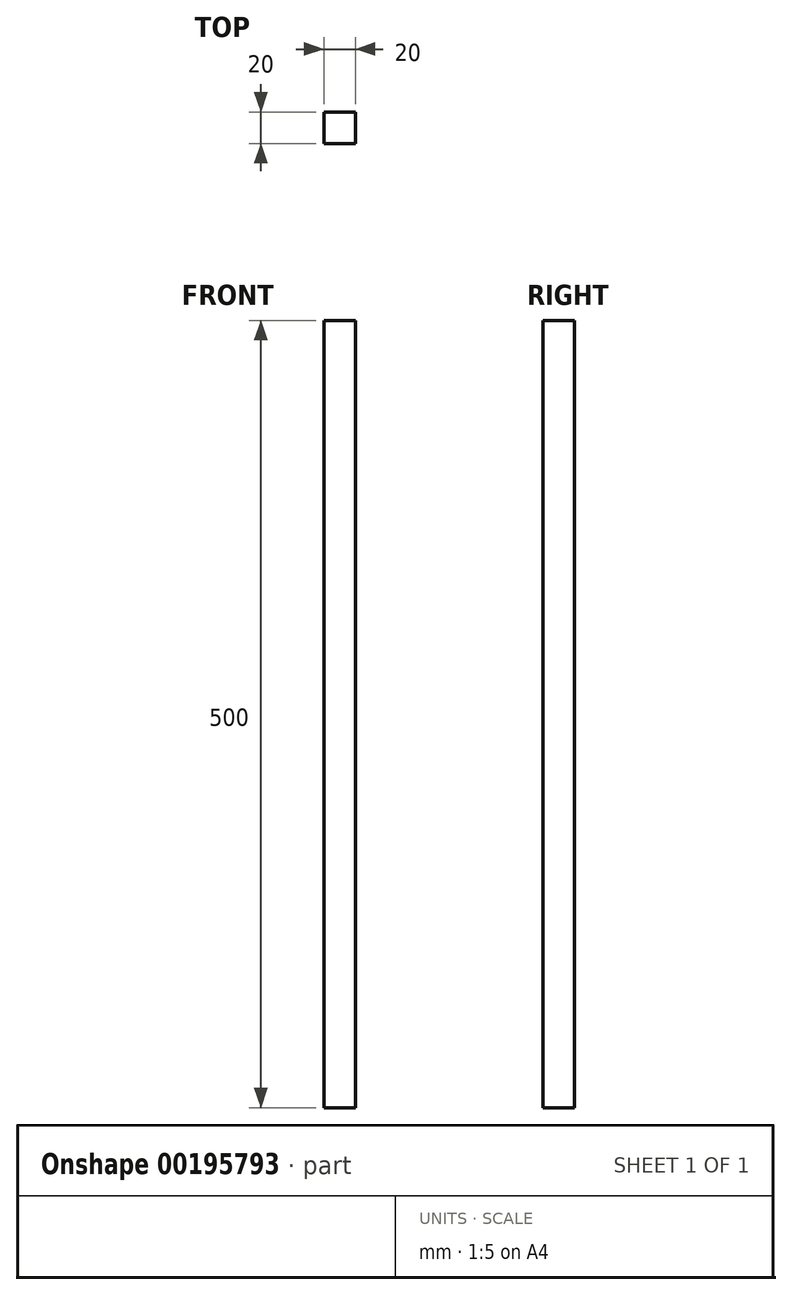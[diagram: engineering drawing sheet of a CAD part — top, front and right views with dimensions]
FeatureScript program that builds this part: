
annotation { "Feature Type Name" : "Feature", "Feature Type Description" : "" }
export const myFeature = defineFeature(function(context is Context, id is Id, definition is map)
    precondition{}
    {
        {
            var Q0;
            Q0=qCreatedBy(makeId("Top.planeOp"),FACE);
            var sketch = newSketch(context, id + "F0", { "sketchPlane" : qUnion([Q0])});
            skLineSegment(sketch, "E0.bottom", {"start": v(-80.54, -42.95) * mm, "end": v(-60.54, -42.95) * mm});
            skLineSegment(sketch, "E0.top", {"start": v(-80.54, -22.95) * mm, "end": v(-60.54, -22.95) * mm});
            skLineSegment(sketch, "E0.left", {"start": v(-80.54, -42.95) * mm, "end": v(-80.54, -22.95) * mm});
            skLineSegment(sketch, "E0.right", {"start": v(-60.54, -42.95) * mm, "end": v(-60.54, -22.95) * mm});
            skSolve(sketch);
        }
        {
            var Q0;
            Q0=makeQuery(id+"F0.imprint","IMPRINT",FACE,{"disambiguationData":[TD([[makeQuery(id+"F0.imprint","IMPRINT",EDGE,{"derivedFrom":sQuery(id+"F0.wireOp",EDGE,"E0.bottom")}),1.0]])]});
            extrude(context, id + "F1", {"entities" : qUnion([Q0]), "depth" : 500 * mm});
        }
    });
